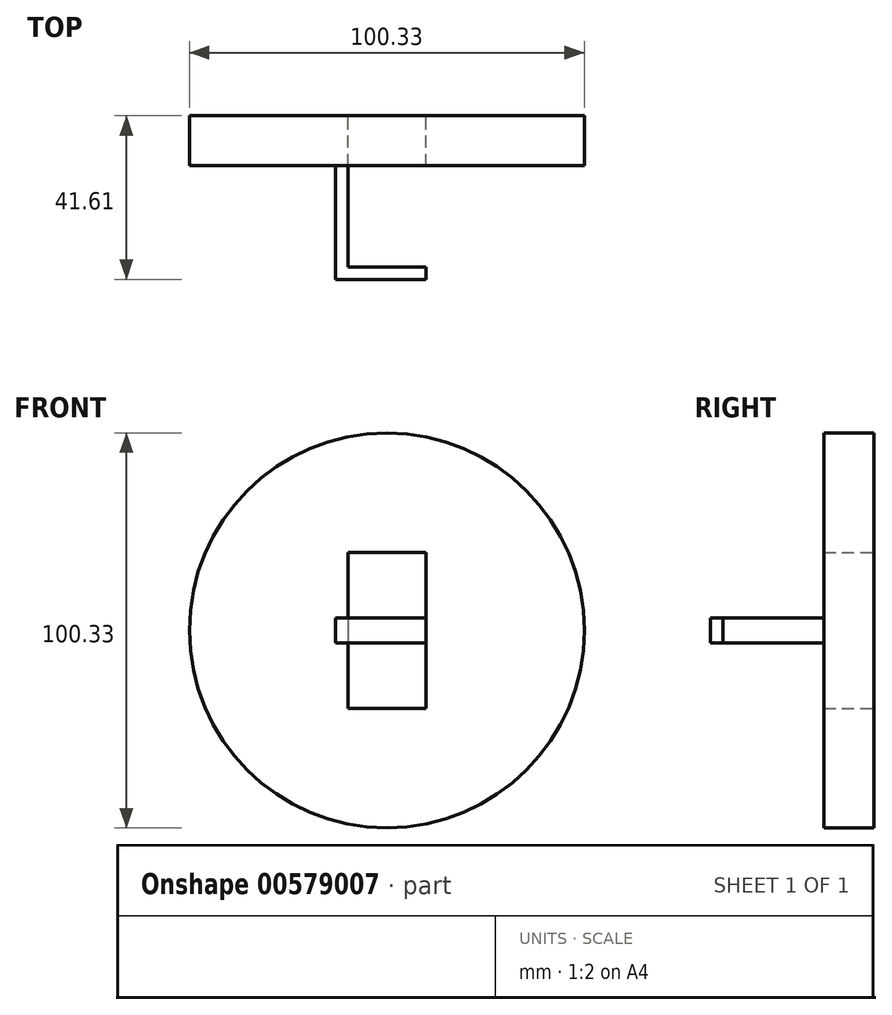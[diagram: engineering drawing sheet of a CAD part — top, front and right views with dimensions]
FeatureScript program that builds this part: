
annotation { "Feature Type Name" : "Feature", "Feature Type Description" : "" }
export const myFeature = defineFeature(function(context is Context, id is Id, definition is map)
    precondition{}
    {
        {
            var Q0;
            Q0=qCreatedBy(makeId("Front.planeOp"),FACE);
            var sketch = newSketch(context, id + "F0", { "sketchPlane" : qUnion([Q0])});
            skLineSegment(sketch, "E0.bottom", {"start": v(-18.54, 17.65) * mm, "end": v(1.27, 17.65) * mm});
            skLineSegment(sketch, "E0.top", {"start": v(-18.54, -21.97) * mm, "end": v(1.27, -21.97) * mm});
            skLineSegment(sketch, "E0.left", {"start": v(-18.54, 17.65) * mm, "end": v(-18.54, -21.97) * mm});
            skLineSegment(sketch, "E0.right", {"start": v(1.27, 17.65) * mm, "end": v(1.27, -21.97) * mm});
            skCircle(sketch, "E1", {"center": v(-8.64, -2.16) * mm, "radius": 50.17 * mm});
            skPoint(sketch, "E1.centerSnap0", {"position": v(-18.54, -2.16) * mm});
            skPoint(sketch, "E1.centerSnap1", {"position": v(-8.64, 17.65) * mm});
            skSolve(sketch);
        }
        {
            var Q0;
            Q0 = qSketchRegion(id + "F0", true);
            extrude(context, id + "F1", {"entities" : qUnion([Q0]), "depth" : 12.7 * mm, "offsetDistance" : 25.4 * mm});
        }
        {
            var Q0;
            Q0=makeQuery(id+"F1.opExtrude","CAP_FACE",FACE,{"disambiguationData":[OSD([sQuery(id+"F0.wireOp",EDGE,"E0.bottom"),sQuery(id+"F0.wireOp",EDGE,"E0.top"),sQuery(id+"F0.wireOp",EDGE,"E0.left"),sQuery(id+"F0.wireOp",EDGE,"E0.right"),sQuery(id+"F0.wireOp",EDGE,"E1")])],"isStart":false});
            var sketch = newSketch(context, id + "F2", { "sketchPlane" : qUnion([Q0])});
            skLineSegment(sketch, "E2.0", {"start": v(-18.54, 17.65) * mm, "end": v(-18.54, -21.97) * mm});
            skLineSegment(sketch, "E3.0", {"start": v(1.27, 17.65) * mm, "end": v(1.27, -21.97) * mm});
            skLineSegment(sketch, "E4.0", {"start": v(-18.54, 17.65) * mm, "end": v(1.27, 17.65) * mm});
            skLineSegment(sketch, "E5.0", {"start": v(-18.54, -21.97) * mm, "end": v(1.27, -21.97) * mm});
            skLineSegment(sketch, "E6.top", {"start": v(-18.54, -5.33) * mm, "end": v(-21.72, -5.33) * mm});
            skLineSegment(sketch, "E6.left", {"start": v(-18.54, -2.16) * mm, "end": v(-18.54, -5.33) * mm});
            skLineSegment(sketch, "E6.right", {"start": v(-21.72, -2.16) * mm, "end": v(-21.72, -5.33) * mm});
            skLineSegment(sketch, "E7.MirrorCS", {"start": v(-21.72, -2.16) * mm, "end": v(-21.72, 1.02) * mm});
            skLineSegment(sketch, "E8.MirrorCS", {"start": v(-18.54, -2.16) * mm, "end": v(-18.54, 1.02) * mm});
            skLineSegment(sketch, "E9.MirrorCS", {"start": v(-18.54, -21.97) * mm, "end": v(-18.54, 17.65) * mm});
            skLineSegment(sketch, "E10.MirrorCS", {"start": v(-18.54, 1.02) * mm, "end": v(-21.72, 1.02) * mm});
            skLineSegment(sketch, "E11", {"start": v(-8.64, 17.65) * mm, "end": v(-8.64, -21.97) * mm, "construction": true});
            skLineSegment(sketch, "E12.MirrorCS", {"start": v(1.27, -2.16) * mm, "end": v(1.27, -5.33) * mm});
            skLineSegment(sketch, "E13.MirrorCS", {"start": v(1.27, 1.02) * mm, "end": v(4.45, 1.02) * mm});
            skLineSegment(sketch, "E14.MirrorCS", {"start": v(4.45, -2.16) * mm, "end": v(4.45, -5.33) * mm});
            skLineSegment(sketch, "E15.MirrorCS", {"start": v(1.27, -5.33) * mm, "end": v(4.45, -5.33) * mm});
            skLineSegment(sketch, "E16.MirrorCS", {"start": v(4.45, -2.16) * mm, "end": v(4.45, 1.02) * mm});
            skLineSegment(sketch, "E17.MirrorCS", {"start": v(1.27, -2.16) * mm, "end": v(1.27, 1.02) * mm});
            skSolve(sketch);
        }
        {
            var Q0;
            {var subQ1=sQuery(id+"F2.wireOp",EDGE,"E6.top");Q0=makeQuery(id+"F2.imprint","IMPRINT",FACE,{"disambiguationData":[TD([[makeQuery(id+"F2.imprint","IMPRINT",EDGE,{"derivedFrom":subQ1}),-1.0]])]});}
            var Q1;
            Q1=makeQuery(id+"F2.imprint","IMPRINT",FACE,{"disambiguationData":[TD([[makeQuery(id+"F2.imprint","IMPRINT",EDGE,{"derivedFrom":sQuery(id+"F2.wireOp",EDGE,"E12.MirrorCS")}),1.0]])]});
            extrude(context, id + "F3", {"entities" : qUnion([Q0, Q1]), "operationType" : NewBodyOperationType.ADD, "depth" : 28.9 * mm, "offsetDistance" : 25.4 * mm});
        }
        {
            var Q0;
            Q0=makeQuery(id+"F3.boolean.opBoolean","MERGE",FACE,{"derivedFrom":[makeQuery(id+"F1.opExtrude","SWEPT_FACE",FACE,{"disambiguationData":[OSD([sQuery(id+"F0.wireOp",EDGE,"E0.left")])]}),makeQuery(id+"F3.opExtrude","SWEPT_FACE",FACE,{"disambiguationData":[OSD([sQuery(id+"F2.wireOp",EDGE,"E9.MirrorCS")])]})]});
            var sketch = newSketch(context, id + "F4", { "sketchPlane" : qUnion([Q0])});
            skLineSegment(sketch, "E18.0", {"start": v(-41.6, 1.02) * mm, "end": v(-41.6, -5.33) * mm});
            skLineSegment(sketch, "E19.0", {"start": v(-41.6, 1.02) * mm, "end": v(-12.7, 1.02) * mm});
            skLineSegment(sketch, "E20.0", {"start": v(-41.6, -5.33) * mm, "end": v(-12.7, -5.33) * mm});
            skLineSegment(sketch, "E21", {"start": v(-41.6, 1.02) * mm, "end": v(-38.43, 1.02) * mm});
            skLineSegment(sketch, "E22", {"start": v(-38.43, 1.02) * mm, "end": v(-38.43, -5.33) * mm});
            skLineSegment(sketch, "E23", {"start": v(-38.43, -5.33) * mm, "end": v(-41.6, -5.33) * mm});
            skSolve(sketch);
        }
        {
            var Q0;
            Q0=makeQuery(id+"F4.imprint","IMPRINT",FACE,{"disambiguationData":[TD([[makeQuery(id+"F4.imprint","IMPRINT",EDGE,{"derivedFrom":sQuery(id+"F4.wireOp",EDGE,"E18.0")}),1.0]])]});
            extrude(context, id + "F5", {"entities" : qUnion([Q0]), "operationType" : NewBodyOperationType.ADD, "depth" : 19.8 * mm, "offsetDistance" : 25.4 * mm});
        }
    });
